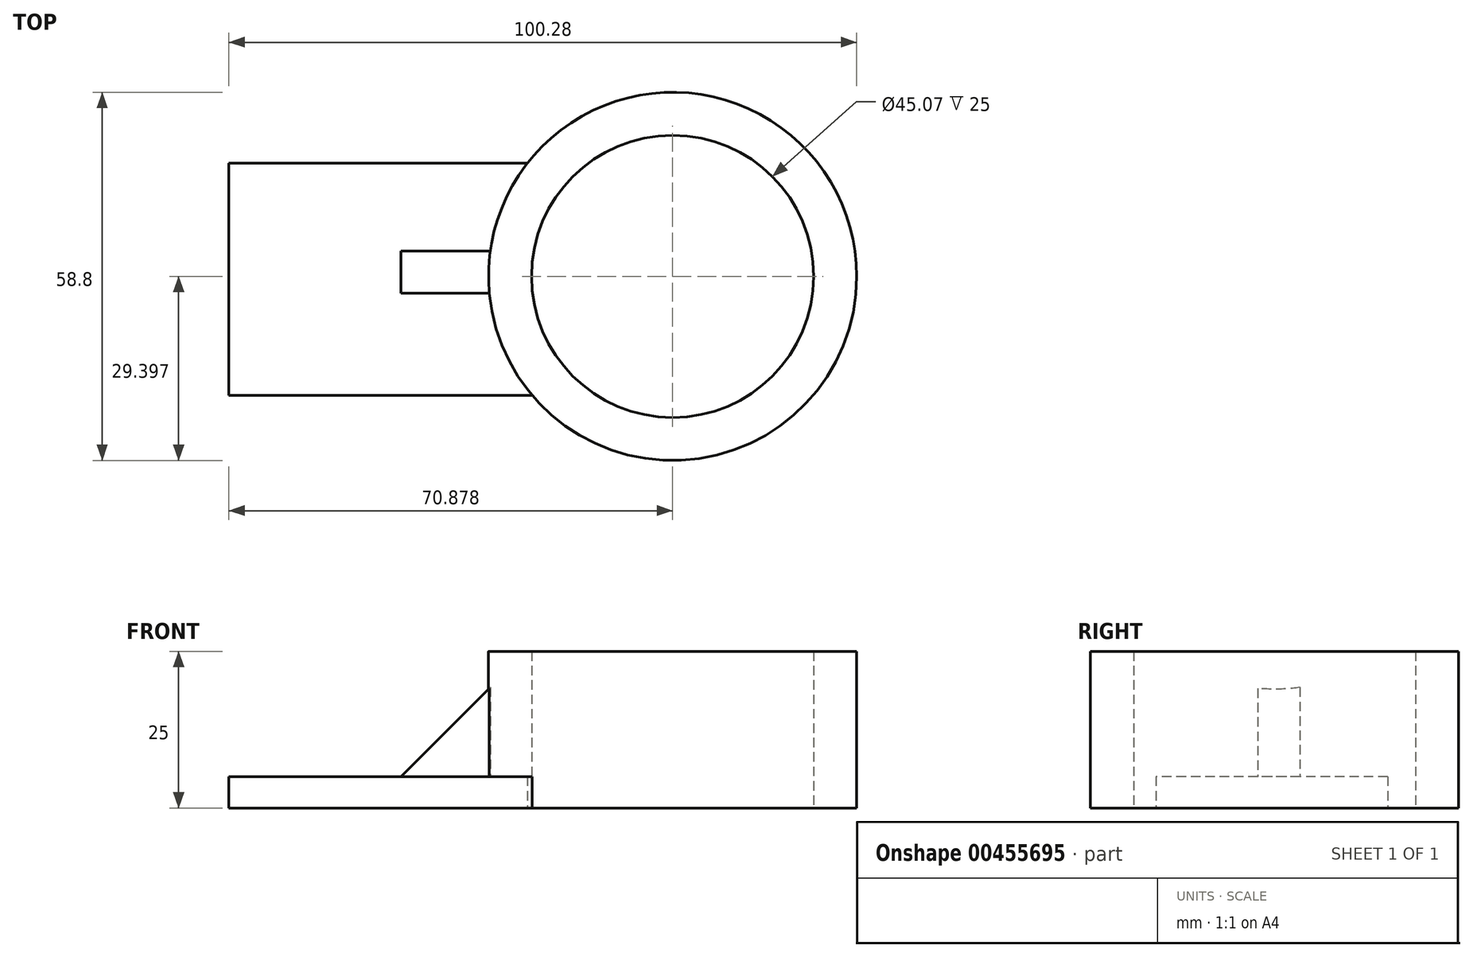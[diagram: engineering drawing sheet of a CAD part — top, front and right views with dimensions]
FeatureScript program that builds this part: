
annotation { "Feature Type Name" : "Feature", "Feature Type Description" : "" }
export const myFeature = defineFeature(function(context is Context, id is Id, definition is map)
    precondition{}
    {
        {
            var Q0;
            Q0=qCreatedBy(makeId("Top.planeOp"),FACE);
            var sketch = newSketch(context, id + "F0", { "sketchPlane" : qUnion([Q0])});
            skCircle(sketch, "E0", {"center": v(43.37, 5.1) * mm, "radius": 29.4 * mm});
            skCircle(sketch, "E1", {"center": v(43.37, 5.1) * mm, "radius": 22.53 * mm});
            skLineSegment(sketch, "E2", {"start": v(20.16, 23.14) * mm, "end": v(-27.5, 23.14) * mm});
            skLineSegment(sketch, "E3", {"start": v(-27.5, 23.14) * mm, "end": v(-27.5, -13.88) * mm});
            skLineSegment(sketch, "E4", {"start": v(-27.5, -13.88) * mm, "end": v(20.92, -13.88) * mm});
            skLineSegment(sketch, "E5", {"start": v(14.25, 9.14) * mm, "end": v(0, 9.14) * mm});
            skLineSegment(sketch, "E6", {"start": v(0, 9.14) * mm, "end": v(0, 2.4) * mm});
            skLineSegment(sketch, "E7", {"start": v(0, 2.4) * mm, "end": v(14.1, 2.4) * mm});
            skSolve(sketch);
        }
        {
            var Q0;
            Q0=makeQuery(id+"F0.imprint","IMPRINT",FACE,{"disambiguationData":[TD([[makeQuery(id+"F0.imprint","IMPRINT",EDGE,{"derivedFrom":sQuery(id+"F0.wireOp",EDGE,"E1")}),-1.0]])]});
            extrude(context, id + "F1", {"entities" : qUnion([Q0]), "depth" : 25 * mm});
        }
        {
            var Q0;
            {var subQ0=sQuery(id+"F0.wireOp",EDGE,"E2");Q0=makeQuery(id+"F0.imprint","IMPRINT",FACE,{"disambiguationData":[TD([[makeQuery(id+"F0.imprint","IMPRINT",EDGE,{"derivedFrom":subQ0}),1.0]])]});}
            extrude(context, id + "F2", {"entities" : qUnion([Q0]), "operationType" : NewBodyOperationType.ADD, "depth" : 5 * mm});
        }
        {
            var Q0;
            {var subQ0=sQuery(id+"F0.wireOp",EDGE,"E5");Q0=makeQuery(id+"F0.imprint","IMPRINT",FACE,{"disambiguationData":[TD([[makeQuery(id+"F0.imprint","IMPRINT",EDGE,{"derivedFrom":subQ0}),1.0]])]});}
            extrude(context, id + "F3", {"entities" : qUnion([Q0]), "operationType" : NewBodyOperationType.ADD, "depth" : 20 * mm});
        }
        {
            var Q0;
            Q0=makeQuery(id+"F3.opExtrude","CAP_EDGE",EDGE,{"disambiguationData":[OSD([sQuery(id+"F0.wireOp",EDGE,"E6")])],"isStart":false});
            chamfer(context, id + "F4", {"entities" : qUnion([Q0]), "width" : 15 * mm, "tangentPropagation" : true});
        }
    });
